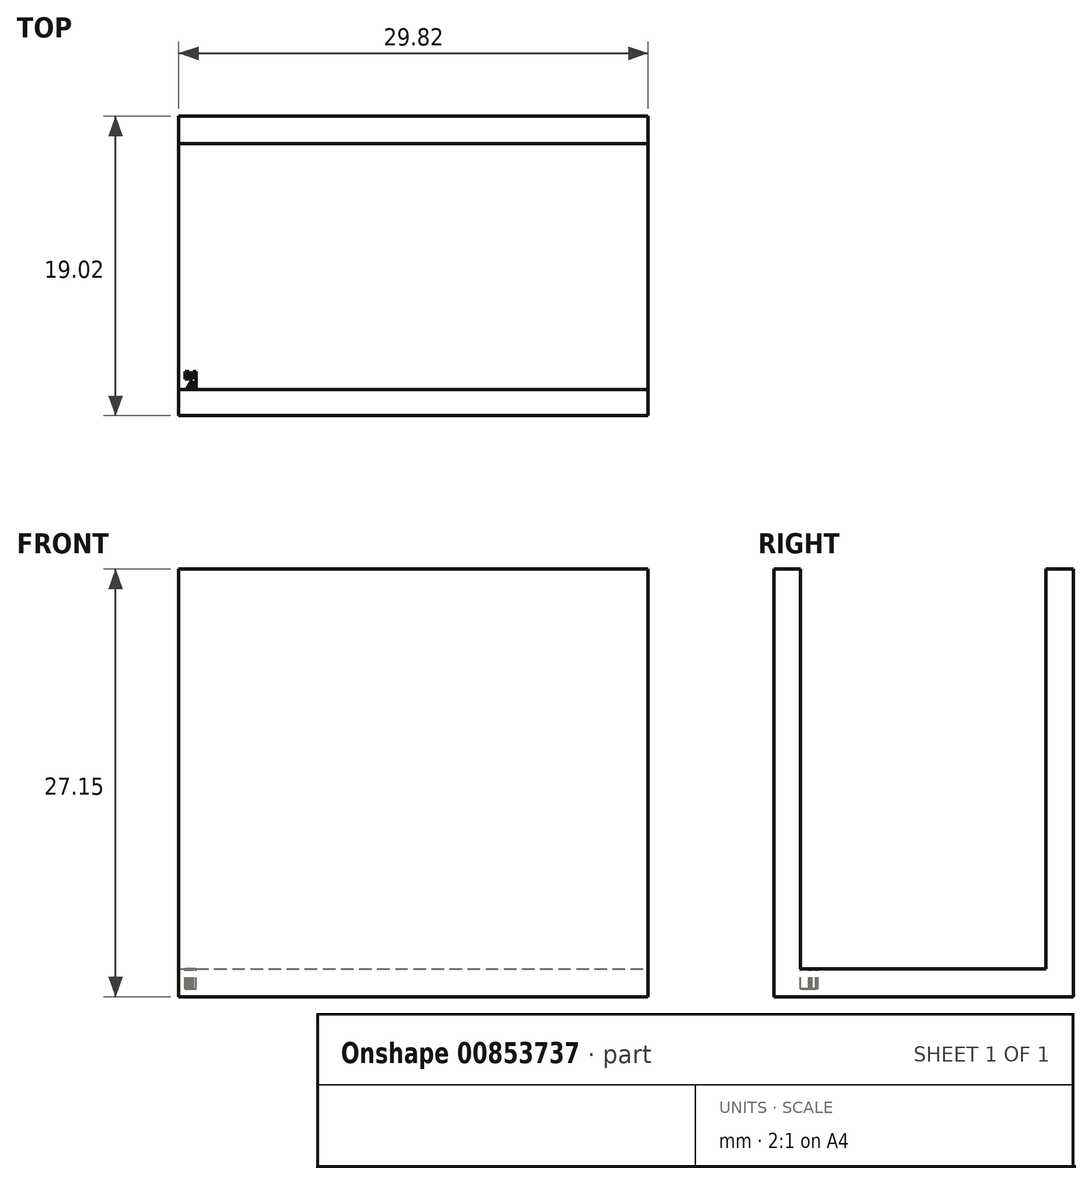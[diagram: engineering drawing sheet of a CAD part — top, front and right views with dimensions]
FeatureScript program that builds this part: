
annotation { "Feature Type Name" : "Feature", "Feature Type Description" : "" }
export const myFeature = defineFeature(function(context is Context, id is Id, definition is map)
    precondition{}
    {
        {
            var Q0;
            Q0=qCreatedBy(makeId("Top.planeOp"),FACE);
            var sketch = newSketch(context, id + "F0", { "sketchPlane" : qUnion([Q0])});
            skLineSegment(sketch, "E0.bottom", {"start": v(-29.82, 19.02) * mm, "end": v(0, 19.02) * mm});
            skLineSegment(sketch, "E0.top", {"start": v(-29.82, 0) * mm, "end": v(0, 0) * mm});
            skLineSegment(sketch, "E0.left", {"start": v(-29.82, 19.02) * mm, "end": v(-29.82, 0) * mm});
            skLineSegment(sketch, "E0.right", {"start": v(0, 19.02) * mm, "end": v(0, 0) * mm});
            skSolve(sketch);
        }
        {
            var Q0;
            Q0=makeQuery(id+"F0.imprint","IMPRINT",FACE,{"disambiguationData":[TD([[makeQuery(id+"F0.imprint","IMPRINT",EDGE,{"derivedFrom":sQuery(id+"F0.wireOp",EDGE,"E0.bottom")}),-1.0]])]});
            extrude(context, id + "F1", {"entities" : qUnion([Q0]), "depth" : 1.75 * mm, "offsetDistance" : 25.4 * mm});
        }
        {
            var Q0;
            Q0=makeQuery(id+"F1.opExtrude","CAP_FACE",FACE,{"disambiguationData":[OSD([sQuery(id+"F0.wireOp",EDGE,"E0.bottom"),sQuery(id+"F0.wireOp",EDGE,"E0.top"),sQuery(id+"F0.wireOp",EDGE,"E0.left"),sQuery(id+"F0.wireOp",EDGE,"E0.right")])],"isStart":false});
            var sketch = newSketch(context, id + "F2", { "sketchPlane" : qUnion([Q0])});
            skLineSegment(sketch, "E1.bottom", {"start": v(-29.82, 1.68) * mm, "end": v(0, 1.68) * mm});
            skLineSegment(sketch, "E1.top", {"start": v(-29.82, 0) * mm, "end": v(0, 0) * mm});
            skLineSegment(sketch, "E1.left", {"start": v(-29.82, 1.68) * mm, "end": v(-29.82, 0) * mm});
            skLineSegment(sketch, "E1.right", {"start": v(0, 1.68) * mm, "end": v(0, 0) * mm});
            skLineSegment(sketch, "E2.bottom", {"start": v(-29.82, 19.02) * mm, "end": v(0, 19.02) * mm});
            skLineSegment(sketch, "E2.top", {"start": v(-29.82, 17.27) * mm, "end": v(0, 17.27) * mm});
            skLineSegment(sketch, "E2.left", {"start": v(-29.82, 19.02) * mm, "end": v(-29.82, 17.27) * mm});
            skLineSegment(sketch, "E2.right", {"start": v(0, 19.02) * mm, "end": v(0, 17.27) * mm});
            skSolve(sketch);
        }
        {
            var Q0;
            Q0 = qSketchRegion(id + "F2", true);
            extrude(context, id + "F3", {"entities" : qUnion([Q0]), "operationType" : NewBodyOperationType.ADD, "depth" : 25.4 * mm, "offsetDistance" : 25.4 * mm});
        }
        {
            var Q0;
            Q0=makeQuery(id+"F1.opExtrude","CAP_FACE",FACE,{"disambiguationData":[OSD([sQuery(id+"F0.wireOp",EDGE,"E0.bottom"),sQuery(id+"F0.wireOp",EDGE,"E0.top"),sQuery(id+"F0.wireOp",EDGE,"E0.left"),sQuery(id+"F0.wireOp",EDGE,"E0.right")])],"isStart":false});
            var sketch = newSketch(context, id + "F4", { "sketchPlane" : qUnion([Q0])});
            skLineSegment(sketch, "E3", {"start": v(-28.7, 1.68) * mm, "end": v(-28.7, 2.8) * mm});
            skLineSegment(sketch, "E4", {"start": v(-28.7, 2.8) * mm, "end": v(-28.9, 2.8) * mm});
            skLineSegment(sketch, "E5", {"start": v(-28.9, 2.8) * mm, "end": v(-28.9, 2.33) * mm});
            skLineSegment(sketch, "E6", {"start": v(-29, 2.2) * mm, "end": v(-29.3, 1.68) * mm});
            skLineSegment(sketch, "E7", {"start": v(-29.3, 1.68) * mm, "end": v(-29.11, 1.68) * mm});
            skLineSegment(sketch, "E8", {"start": v(-29.11, 1.68) * mm, "end": v(-28.86, 2.2) * mm});
            skLineSegment(sketch, "E9", {"start": v(-28.86, 2.2) * mm, "end": v(-28.9, 1.68) * mm});
            skLineSegment(sketch, "E10", {"start": v(-28.9, 1.68) * mm, "end": v(-28.7, 1.68) * mm});
            skLineSegment(sketch, "E11", {"start": v(-28.9, 2.33) * mm, "end": v(-29.17, 2.8) * mm});
            skLineSegment(sketch, "E12", {"start": v(-29.17, 2.8) * mm, "end": v(-29.41, 2.8) * mm});
            skLineSegment(sketch, "E13", {"start": v(-29.41, 2.8) * mm, "end": v(-29.41, 2.33) * mm});
            skLineSegment(sketch, "E14", {"start": v(-29.41, 2.33) * mm, "end": v(-29.2, 2.33) * mm});
            skLineSegment(sketch, "E15", {"start": v(-29.2, 2.33) * mm, "end": v(-29.2, 2.42) * mm});
            skLineSegment(sketch, "E16", {"start": v(-29.2, 2.42) * mm, "end": v(-29.3, 2.42) * mm});
            skLineSegment(sketch, "E17", {"start": v(-29.3, 2.42) * mm, "end": v(-29.3, 2.67) * mm});
            skLineSegment(sketch, "E18", {"start": v(-29.3, 2.67) * mm, "end": v(-29, 2.2) * mm});
            skSolve(sketch);
        }
        {
            var Q0;
            Q0=makeQuery(id+"F4.imprint","IMPRINT",FACE,{"disambiguationData":[TD([[makeQuery(id+"F4.imprint","IMPRINT",EDGE,{"derivedFrom":sQuery(id+"F4.wireOp",EDGE,"E3")}),1.0]])]});
            extrude(context, id + "F5", {"entities" : qUnion([Q0]), "operationType" : NewBodyOperationType.REMOVE, "oppositeDirection" : true, "depth" : 1.27 * mm, "offsetDistance" : 25.4 * mm});
        }
    });
